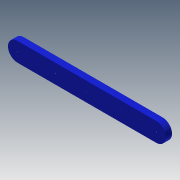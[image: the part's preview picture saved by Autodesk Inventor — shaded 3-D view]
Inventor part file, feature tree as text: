
AUTODESK INVENTOR PART (.ipt)
format: ipt  version: 2013 (Build 170138000, 138)  size: 118,784 bytes
history: native  units: mm
features: extrude x5, sketch x5
ambient origin geometry x8: Origin, YZ Plane, XZ Plane, XY Plane, X Axis, Y Axis, Z Axis, Center Point
bodies: Solid1 (feature_tree)
feature tree (10):
  extrude  "Extrusion1"  Depth=6.0mm
  extrude  "Extrusion2"  Depth=6.0mm
  extrude  "Extrusion3"  Depth=3.0mm
  extrude  "Extrusion4"  Depth=3.0mm
  extrude  "Extrusion5"  Depth=10.0mm
  sketch  "Sketch1"  dims[d0=44.0mm d1=6.0mm]
  sketch  "Sketch2"  dims[d2=6.0mm d3=6.0mm]
  sketch  "Sketch3"  dims[d4=2.0mm d5=0.0mm d6=3.0mm]
  sketch  "Sketch4"  dims[d7=3.0mm d8=3.0mm]
  sketch  "Sketch5"  dims[d9=2.0mm d10=0.0mm d11=10.0mm d12=3.0mm d13=2.0mm d14=0.0mm d15=0.2mm d16=0.2mm d17=0.2mm d18=0.2mm d19=2.0mm d20=0.0mm d21=0.2mm d22=2.0mm d23=0.0mm]
